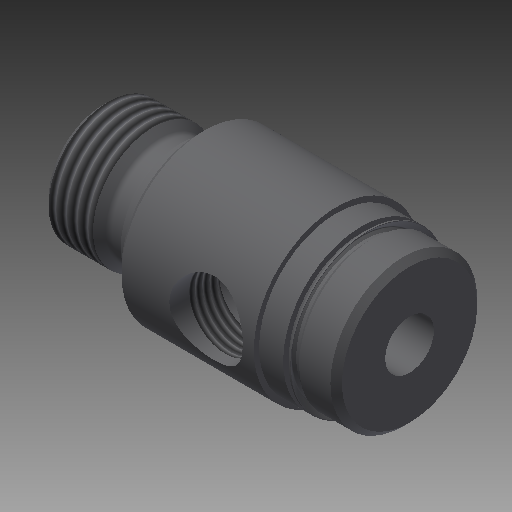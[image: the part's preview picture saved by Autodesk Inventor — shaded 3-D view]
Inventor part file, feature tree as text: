
AUTODESK INVENTOR PART (.ipt)
format: ipt  version: 2018 (Build 220112000, 112)  size: 318,464 bytes
history: native  units: in
note: dims shown in document units (in); Inventor stores cm internally (conversion verified against a paired STEP export)
features: other x119, revolve x6, sketch x6, thread x2
ambient origin geometry x8: Origin, YZ Plane, XZ Plane, XY Plane, X Axis, Y Axis, Z Axis, Center Point
bodies: Solid1 (feature_tree)
feature tree (133):
  revolve  "Revolution1"  [1 undecoded]
  thread  "Thread1"  [1 undecoded]
  revolve  "Revolution2"  Angle=360.0deg
  revolve  "Revolution3"  [1 undecoded]
  revolve  "Revolution4"  [1 undecoded]
  revolve  "Revolution5"  [1 undecoded]
  thread  "Thread2"  [1 undecoded]
  revolve  "Revolution6"  [1 undecoded]
  other  "dp1_XY"
  other  "dp1_YZ"
  other  "dp1_ZX"
  other  "dp1_X"
  other  "dp1_Y"
  other  "dp1_Z"
  other  "dp1_Center"
  other  "dp2_XY"
  other  "dp2_YZ"
  other  "dp2_ZX"
  other  "dp2_X"
  other  "dp2_Y"
  other  "dp2_Z"
  other  "dp2_Center"
  other  "hh_XY"
  other  "hh_YZ"
  other  "hh_ZX"
  other  "hh_X"
  other  "hh_Y"
  other  "hh_Z"
  other  "hh_Center"
  other  "port_XY"
  other  "port_YZ"
  other  "port_ZX"
  other  "port_X"
  other  "port_Y"
  other  "port_Z"
  other  "port_Center"
  other  "rod_guide_XY"
  other  "rod_guide_YZ"
  other  "rod_guide_ZX"
  other  "rod_guide_X"
  other  "rod_guide_Y"
  other  "rod_guide_Z"
  other  "rod_guide_Center"
  other  "s1_XY"
  other  "s1_YZ"
  other  "s1_ZX"
  other  "s1_X"
  other  "s1_Y"
  other  "s1_Z"
  other  "s1_Center"
  other  "s2_XY"
  other  "s2_YZ"
  other  "s2_ZX"
  other  "s2_X"
  other  "s2_Y"
  other  "s2_Z"
  other  "s2_Center"
  other  "t1_XY"
  other  "t1_YZ"
  other  "t1_ZX"
  other  "t1_X"
  other  "t1_Y"
  other  "t1_Z"
  other  "t1_Center"
  other  "t111_XY"
  other  "t111_YZ"
  other  "t111_ZX"
  other  "t111_X"
  other  "t111_Y"
  other  "t111_Z"
  other  "t111_Center"
  other  "to_foot_bracket_XY"
  other  "to_foot_bracket_YZ"
  other  "to_foot_bracket_ZX"
  other  "to_foot_bracket_X"
  other  "to_foot_bracket_Y"
  other  "to_foot_bracket_Z"
  other  "to_foot_bracket_Center"
  other  "to_nut_XY"
  other  "to_nut_YZ"
  other  "to_nut_ZX"
  other  "to_nut_X"
  other  "to_nut_Y"
  other  "to_nut_Z"
  other  "to_nut_Center"
  other  "to_rod_XY"
  other  "to_rod_YZ"
  other  "to_rod_ZX"
  other  "to_rod_X"
  other  "to_rod_Y"
  other  "to_rod_Z"
  other  "to_rod_Center"
  other  "to_screw_XY"
  other  "to_screw_YZ"
  other  "to_screw_ZX"
  other  "to_screw_X"
  other  "to_screw_Y"
  other  "to_screw_Z"
  other  "to_screw_Center"
  other  "to_trunnion_brackets_XY"
  other  "to_trunnion_brackets_YZ"
  other  "to_trunnion_brackets_ZX"
  other  "to_trunnion_brackets_X"
  other  "to_trunnion_brackets_Y"
  other  "to_trunnion_brackets_Z"
  other  "to_trunnion_brackets_Center"
  other  "to_trunnion_brackets1_XY"
  other  "to_trunnion_brackets1_YZ"
  other  "to_trunnion_brackets1_ZX"
  other  "to_trunnion_brackets1_X"
  other  "to_trunnion_brackets1_Y"
  other  "to_trunnion_brackets1_Z"
  other  "to_trunnion_brackets1_Center"
  other  "to_trunnion_brackets2_XY"
  other  "to_trunnion_brackets2_YZ"
  other  "to_trunnion_brackets2_ZX"
  other  "to_trunnion_brackets2_X"
  other  "to_trunnion_brackets2_Y"
  other  "to_trunnion_brackets2_Z"
  other  "to_trunnion_brackets2_Center"
  other  "to_tube_XY"
  other  "to_tube_YZ"
  other  "to_tube_ZX"
  other  "to_tube_X"
  other  "to_tube_Y"
  other  "to_tube_Z"
  other  "to_tube_Center"
  sketch  "Sketch_2"  dims[d4=360.0deg d5=360.0deg]
  sketch  "Sketch_3"  dims[d6=360.0deg d7=0.1501in d8=0.0in]
  sketch  "Sketch_5_ALT_Drilling_1"  dims[d0=360.0deg d1=0.23in d2=0.0in d3=360.0deg]
  sketch  "Sketch_10"  dims[d9=360.0deg]
  sketch  "Sketch_40"  dims[d10=0.0in d11=0.0in d12=0.0in d13=0.0in d14=0.0in d15=0.0in]
  sketch  "Sketch_47"
note: 7 required parameter values undecoded (feature->parameter linkage not recoverable at this tier; creation-order binding heuristic only, values carry confidence <= 0.55)